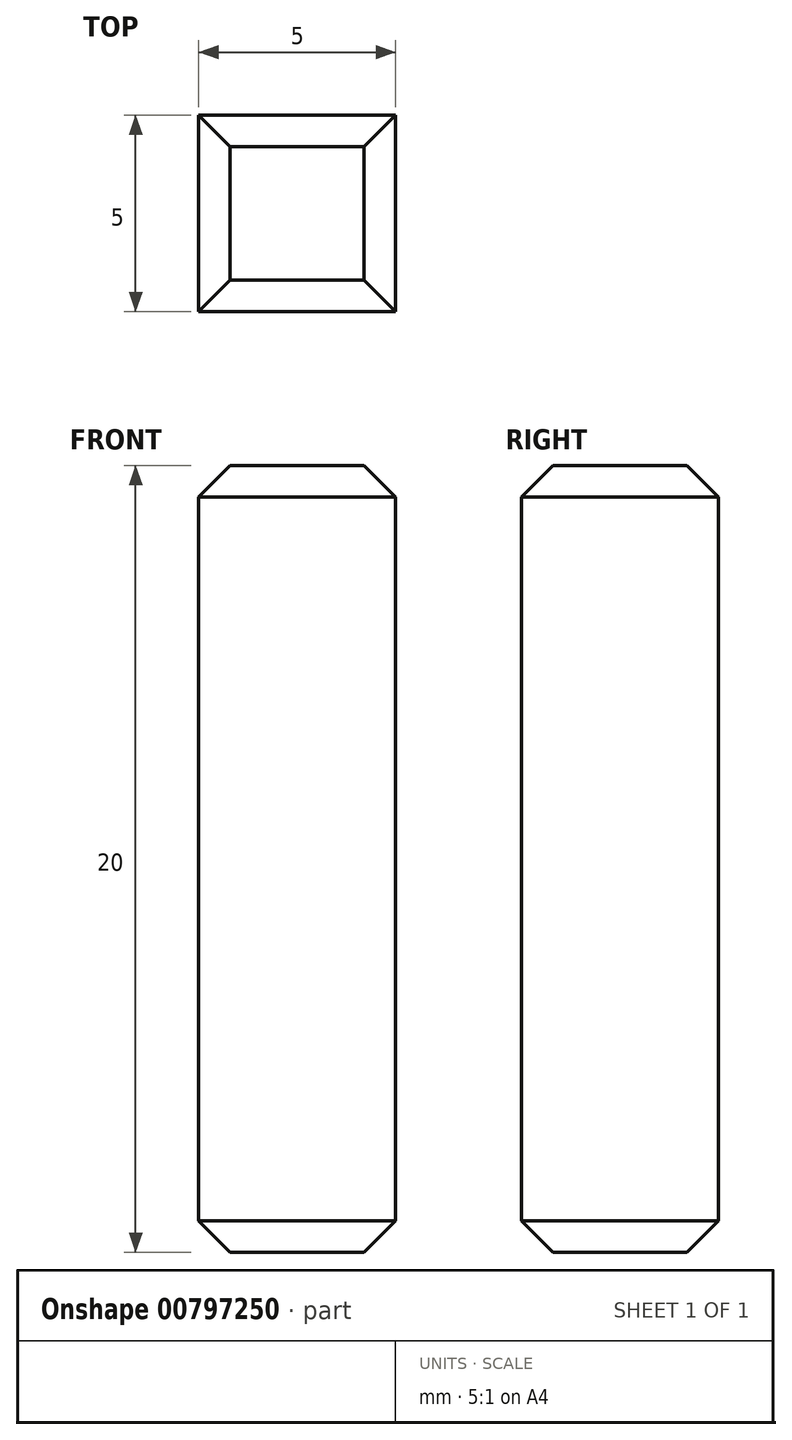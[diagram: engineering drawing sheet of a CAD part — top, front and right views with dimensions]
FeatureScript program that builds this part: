
annotation { "Feature Type Name" : "Feature", "Feature Type Description" : "" }
export const myFeature = defineFeature(function(context is Context, id is Id, definition is map)
    precondition{}
    {
        {
            var Q0;
            Q0=qCreatedBy(makeId("Top.planeOp"),FACE);
            var sketch = newSketch(context, id + "F0", { "sketchPlane" : qUnion([Q0])});
            skLineSegment(sketch, "E0.bottom", {"start": v(-2.5, -2.5) * mm, "end": v(2.5, -2.5) * mm});
            skLineSegment(sketch, "E0.top", {"start": v(-2.5, 2.5) * mm, "end": v(2.5, 2.5) * mm});
            skLineSegment(sketch, "E0.left", {"start": v(-2.5, -2.5) * mm, "end": v(-2.5, 2.5) * mm});
            skLineSegment(sketch, "E0.right", {"start": v(2.5, -2.5) * mm, "end": v(2.5, 2.5) * mm});
            skPoint(sketch, "E0.middle", {"position": v(0, 0) * mm});
            skSolve(sketch);
        }
        {
            var Q0;
            Q0 = qSketchRegion(id + "F0", true);
            extrude(context, id + "F1", {"entities" : qUnion([Q0]), "depth" : 20 * mm, "offsetDistance" : 25 * mm});
        }
        {
            var Q0;
            Q0=makeQuery(id+"F1.opExtrude","CAP_FACE",FACE,{"disambiguationData":[OSD([sQuery(id+"F0.wireOp",EDGE,"E0.bottom"),sQuery(id+"F0.wireOp",EDGE,"E0.top"),sQuery(id+"F0.wireOp",EDGE,"E0.left"),sQuery(id+"F0.wireOp",EDGE,"E0.right")])],"isStart":false});
            var Q1;
            Q1=makeQuery(id+"F1.opExtrude","CAP_FACE",FACE,{"disambiguationData":[OSD([sQuery(id+"F0.wireOp",EDGE,"E0.bottom"),sQuery(id+"F0.wireOp",EDGE,"E0.top"),sQuery(id+"F0.wireOp",EDGE,"E0.left"),sQuery(id+"F0.wireOp",EDGE,"E0.right")])],"isStart":true});
            chamfer(context, id + "F2", {"entities" : qUnion([Q0, Q1]), "width" : .8 * mm, "tangentPropagation" : true});
        }
    });
